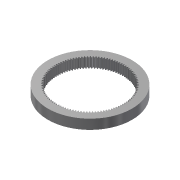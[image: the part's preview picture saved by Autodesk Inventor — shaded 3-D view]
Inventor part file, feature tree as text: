
AUTODESK INVENTOR PART (.ipt)
format: ipt  version: 2018 (Build 220112000, 112)  size: 1,501,184 bytes
history: native  units: mm (DEFAULTED — no unit token found)
features: other x4, plane x3, sketch x3, extrude x2
ambient origin geometry x8: Origin, YZ Plane, XZ Plane, XY Plane, X Axis, Y Axis, Z Axis, Center Point
bodies: Solid1 (feature_tree)
feature tree (12):
  extrude  "Extrusion1"  Depth=15.0mm TaperAngle=0.0deg
  plane  "Work Plane2"
  plane  "Work Plane8"
  plane  "Work Plane9"
  other  "正齒輪"
  extrude  "擠出2"  Depth=10.0mm TaperAngle=0.0deg
  sketch  "Sketch1"  dims[d0=107.0mm d1=15.0mm d2=0.0mm]
  sketch  "Sketch2"  dims[d3=105.0mm d4=10.0mm d5=0.0mm d16=81.0mm d17=0.0mm d34=0.299199mm d39=0.0mm d41=0.0mm d43=81.0mm d46=81.0mm d47=0.0mm d48=0.0mm d49=130.0mm d50=15.0mm d51=0.0mm]
  other  "Srf1"
  sketch  "草圖4"
  other  "實體2"
  other  "節圓直徑"
